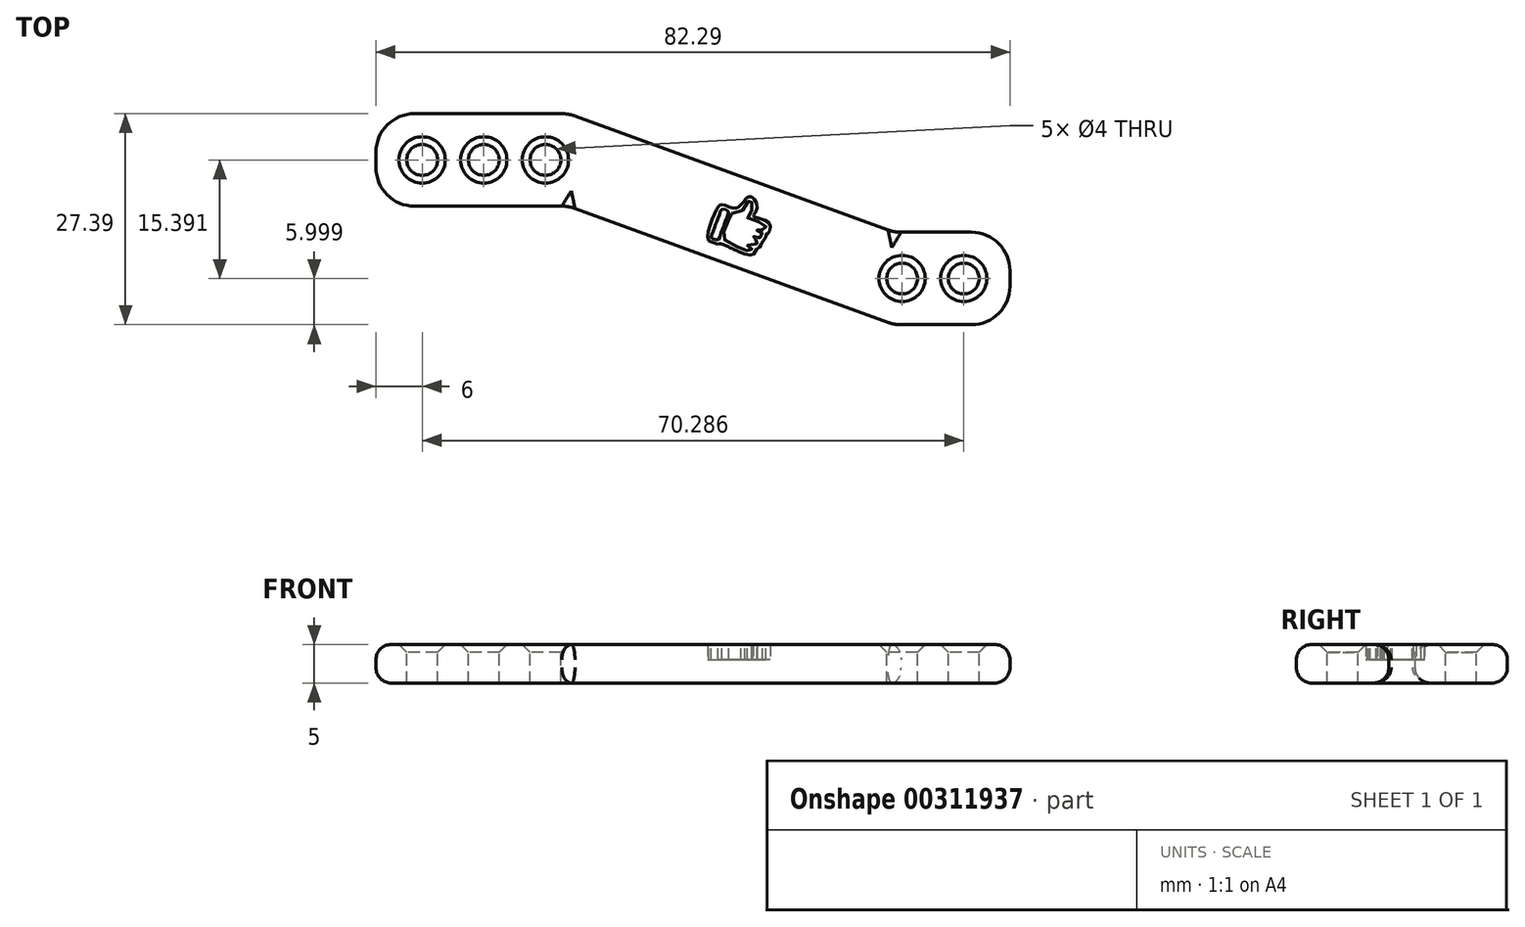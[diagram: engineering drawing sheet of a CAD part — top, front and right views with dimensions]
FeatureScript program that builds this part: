
annotation { "Feature Type Name" : "Feature", "Feature Type Description" : "" }
export const myFeature = defineFeature(function(context is Context, id is Id, definition is map)
    precondition{}
    {
        {
            var Q0;
            Q0=qCreatedBy(makeId("Top.planeOp"),FACE);
            var sketch = newSketch(context, id + "F0", { "sketchPlane" : qUnion([Q0])});
            skLineSegment(sketch, "E0.bottom", {"start": v(0, 12) * mm, "end": v(25, 12) * mm});
            skLineSegment(sketch, "E0.top", {"start": v(0, 0) * mm, "end": v(25, 0) * mm});
            skLineSegment(sketch, "E0.left", {"start": v(0, 12) * mm, "end": v(0, 0) * mm});
            skLineSegment(sketch, "E0.right", {"start": v(25, 12) * mm, "end": v(25, 0) * mm});
            skLineSegment(sketch, "E1.bottom", {"start": v(67.29, -3.4) * mm, "end": v(82.29, -3.4) * mm});
            skLineSegment(sketch, "E1.top", {"start": v(67.29, -15.4) * mm, "end": v(82.29, -15.4) * mm});
            skLineSegment(sketch, "E1.left", {"start": v(67.29, -3.4) * mm, "end": v(67.29, -15.4) * mm});
            skLineSegment(sketch, "E1.right", {"start": v(82.29, -3.4) * mm, "end": v(82.29, -15.4) * mm});
            skLineSegment(sketch, "E2", {"start": v(25, 12) * mm, "end": v(67.29, -3.4) * mm});
            skLineSegment(sketch, "E3", {"start": v(25, 0) * mm, "end": v(67.29, -15.4) * mm});
            skSolve(sketch);
        }
        {
            var Q0;
            Q0=makeQuery(id+"F0.imprint","IMPRINT",FACE,{"disambiguationData":[TD([[makeQuery(id+"F0.imprint","IMPRINT",EDGE,{"derivedFrom":sQuery(id+"F0.wireOp",EDGE,"E0.bottom")}),-1.0]])]});
            var Q1;
            Q1=makeQuery(id+"F0.imprint","IMPRINT",FACE,{"disambiguationData":[TD([[makeQuery(id+"F0.imprint","IMPRINT",EDGE,{"derivedFrom":sQuery(id+"F0.wireOp",EDGE,"E0.right")}),1.0]])]});
            var Q2;
            Q2=makeQuery(id+"F0.imprint","IMPRINT",FACE,{"disambiguationData":[TD([[makeQuery(id+"F0.imprint","IMPRINT",EDGE,{"derivedFrom":sQuery(id+"F0.wireOp",EDGE,"E1.bottom")}),-1.0]])]});
            extrude(context, id + "F1", {"entities" : qUnion([Q0, Q1, Q2]), "depth" : 5 * mm});
        }
        {
            var Q0;
            Q0=makeQuery(id+"F1.opExtrude","CAP_FACE",FACE,{"disambiguationData":[OSD([sQuery(id+"F0.wireOp",EDGE,"E0.bottom"),sQuery(id+"F0.wireOp",EDGE,"E0.top"),sQuery(id+"F0.wireOp",EDGE,"E0.left"),sQuery(id+"F0.wireOp",EDGE,"E1.bottom"),sQuery(id+"F0.wireOp",EDGE,"E1.top"),sQuery(id+"F0.wireOp",EDGE,"E1.right"),sQuery(id+"F0.wireOp",EDGE,"E2"),sQuery(id+"F0.wireOp",EDGE,"E3")])],"isStart":false});
            var sketch = newSketch(context, id + "F2", { "sketchPlane" : qUnion([Q0])});
            skCircle(sketch, "E4", {"center": v(6, 6) * mm, "radius": 2 * mm});
            skCircle(sketch, "E5", {"center": v(76.29, -9.4) * mm, "radius": 2 * mm});
            skCircle(sketch, "E6.1.0.0", {"center": v(14, 6) * mm, "radius": 2 * mm});
            skCircle(sketch, "E6.2.0.0", {"center": v(22, 6) * mm, "radius": 2 * mm});
            skLineSegment(sketch, "E6.direction1", {"start": v(6, 6) * mm, "end": v(14, 6) * mm, "construction": true});
            skCircle(sketch, "E7.1.0.0", {"center": v(68.29, -9.4) * mm, "radius": 2 * mm});
            skLineSegment(sketch, "E7.direction1", {"start": v(76.29, -9.4) * mm, "end": v(68.29, -9.4) * mm, "construction": true});
            skSolve(sketch);
        }
        {
            var Q0;
            Q0 = qSketchRegion(id + "F2", true);
            extrude(context, id + "F3", {"entities" : qUnion([Q0]), "operationType" : NewBodyOperationType.REMOVE, "endBound" : BoundingType.THROUGH_ALL, "oppositeDirection" : true, "depth" : 5 * mm});
        }
        {
            var Q0;
            Q0=makeQuery(id+"F1.opExtrude","CAP_EDGE",EDGE,{"disambiguationData":[OSD([sQuery(id+"F0.wireOp",EDGE,"E0.left")])],"isStart":false});
            var Q1;
            Q1=makeQuery(id+"F1.opExtrude","CAP_EDGE",EDGE,{"disambiguationData":[OSD([sQuery(id+"F0.wireOp",EDGE,"E0.top")])],"isStart":false});
            var Q2;
            Q2=makeQuery(id+"F1.opExtrude","CAP_EDGE",EDGE,{"disambiguationData":[OSD([sQuery(id+"F0.wireOp",EDGE,"E3")])],"isStart":false});
            var Q3;
            Q3=makeQuery(id+"F1.opExtrude","CAP_EDGE",EDGE,{"disambiguationData":[OSD([sQuery(id+"F0.wireOp",EDGE,"E1.top")])],"isStart":false});
            var Q4;
            Q4=makeQuery(id+"F1.opExtrude","CAP_EDGE",EDGE,{"disambiguationData":[OSD([sQuery(id+"F0.wireOp",EDGE,"E1.right")])],"isStart":false});
            var Q5;
            Q5=makeQuery(id+"F1.opExtrude","CAP_EDGE",EDGE,{"disambiguationData":[OSD([sQuery(id+"F0.wireOp",EDGE,"E1.bottom")])],"isStart":false});
            var Q6;
            Q6=makeQuery(id+"F1.opExtrude","CAP_EDGE",EDGE,{"disambiguationData":[OSD([sQuery(id+"F0.wireOp",EDGE,"E2")])],"isStart":false});
            var Q7;
            Q7=makeQuery(id+"F1.opExtrude","CAP_EDGE",EDGE,{"disambiguationData":[OSD([sQuery(id+"F0.wireOp",EDGE,"E0.bottom")])],"isStart":false});
            var Q8;
            Q8=makeQuery(id+"F1.opExtrude","CAP_EDGE",EDGE,{"disambiguationData":[OSD([sQuery(id+"F0.wireOp",EDGE,"E1.top")])],"isStart":true});
            var Q9;
            Q9=makeQuery(id+"F1.opExtrude","CAP_EDGE",EDGE,{"disambiguationData":[OSD([sQuery(id+"F0.wireOp",EDGE,"E1.right")])],"isStart":true});
            var Q10;
            Q10=makeQuery(id+"F1.opExtrude","CAP_EDGE",EDGE,{"disambiguationData":[OSD([sQuery(id+"F0.wireOp",EDGE,"E1.bottom")])],"isStart":true});
            var Q11;
            Q11=makeQuery(id+"F1.opExtrude","CAP_EDGE",EDGE,{"disambiguationData":[OSD([sQuery(id+"F0.wireOp",EDGE,"E2")])],"isStart":true});
            var Q12;
            Q12=makeQuery(id+"F1.opExtrude","CAP_EDGE",EDGE,{"disambiguationData":[OSD([sQuery(id+"F0.wireOp",EDGE,"E3")])],"isStart":true});
            var Q13;
            Q13=makeQuery(id+"F1.opExtrude","CAP_EDGE",EDGE,{"disambiguationData":[OSD([sQuery(id+"F0.wireOp",EDGE,"E0.top")])],"isStart":true});
            var Q14;
            Q14=makeQuery(id+"F1.opExtrude","CAP_EDGE",EDGE,{"disambiguationData":[OSD([sQuery(id+"F0.wireOp",EDGE,"E0.left")])],"isStart":true});
            var Q15;
            Q15=makeQuery(id+"F1.opExtrude","CAP_EDGE",EDGE,{"disambiguationData":[OSD([sQuery(id+"F0.wireOp",EDGE,"E0.bottom")])],"isStart":true});
            fillet(context, id + "F4", {"entities" : qUnion([Q0, Q1, Q2, Q3, Q4, Q5, Q6, Q7, Q8, Q9, Q10, Q11, Q12, Q13, Q14, Q15]), "radius" : 2 * mm, "tangentPropagation" : true, "allowEdgeOverflow" : false});
        }
        {
            var Q0;
            Q0=makeQuery(id+"F1.opExtrude","SWEPT_EDGE",EDGE,{"disambiguationData":[OSD([sQuery(id+"F0.wireOp",EDGE,"E0.top"),sQuery(id+"F0.wireOp",EDGE,"E0.left")])]});
            var Q1;
            Q1=makeQuery(id+"F1.opExtrude","SWEPT_EDGE",EDGE,{"disambiguationData":[OSD([sQuery(id+"F0.wireOp",EDGE,"E0.top"),sQuery(id+"F0.wireOp",EDGE,"E0.right"),sQuery(id+"F0.wireOp",EDGE,"E3")])]});
            var Q2;
            Q2=makeQuery(id+"F1.opExtrude","SWEPT_EDGE",EDGE,{"disambiguationData":[OSD([sQuery(id+"F0.wireOp",EDGE,"E1.top"),sQuery(id+"F0.wireOp",EDGE,"E1.left"),sQuery(id+"F0.wireOp",EDGE,"E3")])]});
            var Q3;
            Q3=makeQuery(id+"F1.opExtrude","SWEPT_EDGE",EDGE,{"disambiguationData":[OSD([sQuery(id+"F0.wireOp",EDGE,"E1.top"),sQuery(id+"F0.wireOp",EDGE,"E1.right")])]});
            var Q4;
            Q4=makeQuery(id+"F1.opExtrude","SWEPT_EDGE",EDGE,{"disambiguationData":[OSD([sQuery(id+"F0.wireOp",EDGE,"E1.bottom"),sQuery(id+"F0.wireOp",EDGE,"E1.right")])]});
            var Q5;
            Q5=makeQuery(id+"F1.opExtrude","SWEPT_EDGE",EDGE,{"disambiguationData":[OSD([sQuery(id+"F0.wireOp",EDGE,"E1.bottom"),sQuery(id+"F0.wireOp",EDGE,"E1.left"),sQuery(id+"F0.wireOp",EDGE,"E2")])]});
            var Q6;
            Q6=makeQuery(id+"F1.opExtrude","SWEPT_EDGE",EDGE,{"disambiguationData":[OSD([sQuery(id+"F0.wireOp",EDGE,"E0.bottom"),sQuery(id+"F0.wireOp",EDGE,"E0.right"),sQuery(id+"F0.wireOp",EDGE,"E2")])]});
            var Q7;
            Q7=makeQuery(id+"F1.opExtrude","SWEPT_EDGE",EDGE,{"disambiguationData":[OSD([sQuery(id+"F0.wireOp",EDGE,"E0.bottom"),sQuery(id+"F0.wireOp",EDGE,"E0.left")])]});
            fillet(context, id + "F5", {"entities" : qUnion([Q0, Q1, Q2, Q3, Q4, Q5, Q6, Q7]), "radius" : 5 * mm, "tangentPropagation" : true, "allowEdgeOverflow" : false});
        }
        {
            var Q0;
            Q0=makeQuery(id+"F1.opExtrude","CAP_FACE",FACE,{"disambiguationData":[OSD([sQuery(id+"F0.wireOp",EDGE,"E0.bottom"),sQuery(id+"F0.wireOp",EDGE,"E0.top"),sQuery(id+"F0.wireOp",EDGE,"E0.left"),sQuery(id+"F0.wireOp",EDGE,"E1.bottom"),sQuery(id+"F0.wireOp",EDGE,"E1.top"),sQuery(id+"F0.wireOp",EDGE,"E1.right"),sQuery(id+"F0.wireOp",EDGE,"E2"),sQuery(id+"F0.wireOp",EDGE,"E3")])],"isStart":false});
            chamfer(context, id + "F6", {"entities" : qUnion([Q0]), "width" : 1 * mm, "tangentPropagation" : true});
        }
        {
            var Q0;
            Q0=makeQuery(id+"F1.opExtrude","CAP_FACE",FACE,{"disambiguationData":[OSD([sQuery(id+"F0.wireOp",EDGE,"E0.bottom"),sQuery(id+"F0.wireOp",EDGE,"E0.top"),sQuery(id+"F0.wireOp",EDGE,"E0.left"),sQuery(id+"F0.wireOp",EDGE,"E1.bottom"),sQuery(id+"F0.wireOp",EDGE,"E1.top"),sQuery(id+"F0.wireOp",EDGE,"E1.right"),sQuery(id+"F0.wireOp",EDGE,"E2"),sQuery(id+"F0.wireOp",EDGE,"E3")])],"isStart":false});
            var sketch = newSketch(context, id + "F7", { "sketchPlane" : qUnion([Q0])});
            skPoint(sketch, "E8", {"position": v(46.25, -5.6) * mm});
            skFitSpline(sketch, "E9", {"points": [v(48.74, 1.23) * mm, v(49.44, 0.27) * mm, v(49.2, -0.9) * mm, v(48.97, -1.3) * mm, v(50.7, -1.92) * mm, v(51.18, -2.7) * mm, v(50.86, -3.57) * mm, v(50.67, -3.59) * mm, v(50.54, -4.12) * mm, v(50.15, -4.62) * mm, v(49.87, -5.25) * mm, v(49.3, -5.67) * mm, v(49.07, -6.21) * mm, v(47.89, -6.2) * mm, v(44.84, -4.91) * mm, v(44.37, -4.92) * mm, v(43.15, -4.48) * mm, v(44.18, -0.52) * mm, v(44.8, 0.17) * mm, v(45.67, -0.03) * mm, v(46.25, -0.23) * mm, v(47.22, 0) * mm, v(48.1, 1.07) * mm, v(48.52, 1.22) * mm, v(48.74, 1.23) * mm]});
            skFitSpline(sketch, "E10", {"points": [v(46.14, -0.95) * mm, v(47.17, -0.73) * mm, v(47.96, -0.05) * mm, v(48.34, 0.7) * mm, v(48.48, 0.8) * mm, v(48.67, 0.68) * mm, v(48.85, 0.28) * mm, v(48.87, -0.32) * mm, v(48.61, -0.9) * mm, v(48.23, -1.5) * mm, v(48.9, -1.76) * mm, v(50.13, -2.26) * mm, v(50.59, -2.51) * mm, v(50.6, -2.86) * mm, v(50.38, -3.12) * mm, v(50.03, -3.07) * mm, v(49.53, -2.93) * mm, v(49.44, -3.04) * mm, v(49.51, -3.19) * mm, v(49.87, -3.35) * mm, v(50.13, -3.48) * mm, v(50.16, -3.76) * mm, v(50.03, -3.98) * mm, v(49.75, -4.12) * mm, v(49.43, -4.11) * mm, v(48.99, -3.95) * mm, v(48.82, -4.04) * mm, v(48.95, -4.22) * mm, v(49.34, -4.35) * mm, v(49.5, -4.54) * mm, v(49.55, -4.7) * mm, v(49.3, -5) * mm, v(48.95, -5.07) * mm, v(48.64, -5.02) * mm, v(48.33, -4.9) * mm, v(48.23, -4.94) * mm, v(48.19, -5.06) * mm, v(48.42, -5.23) * mm, v(48.77, -5.39) * mm, v(48.75, -5.6) * mm, v(48.53, -5.82) * mm, v(48.23, -5.79) * mm, v(47.89, -5.67) * mm, v(46.8, -5.24) * mm, v(45.29, -4.42) * mm, v(44.92, -4.09) * mm, v(45.33, -2.92) * mm, v(45.68, -1.96) * mm, v(45.95, -1.2) * mm, v(46.14, -0.95) * mm]});
            skFitSpline(sketch, "E11", {"points": [v(44.95, -0.35) * mm, v(45.64, -0.6) * mm, v(45.75, -0.82) * mm, v(45.53, -1.5) * mm, v(45.3, -2.12) * mm, v(45.07, -2.8) * mm, v(44.7, -3.74) * mm, v(44.48, -4.3) * mm, v(44.32, -4.38) * mm, v(43.6, -4.16) * mm, v(43.51, -3.9) * mm, v(43.8, -3.15) * mm, v(44.1, -2.33) * mm, v(44.34, -1.73) * mm, v(44.61, -0.95) * mm, v(44.95, -0.35) * mm]});
            skSolve(sketch);
        }
        {
            var Q0;
            Q0=makeQuery(id+"F7.imprint","IMPRINT",FACE,{"disambiguationData":[TD([[makeQuery(id+"F7.imprint","IMPRINT",EDGE,{"derivedFrom":sQuery(id+"F7.wireOp",EDGE,"E10")}),1.0]])]});
            extrude(context, id + "F8", {"entities" : qUnion([Q0]), "operationType" : NewBodyOperationType.REMOVE, "oppositeDirection" : true, "depth" : 2 * mm});
        }
    });
